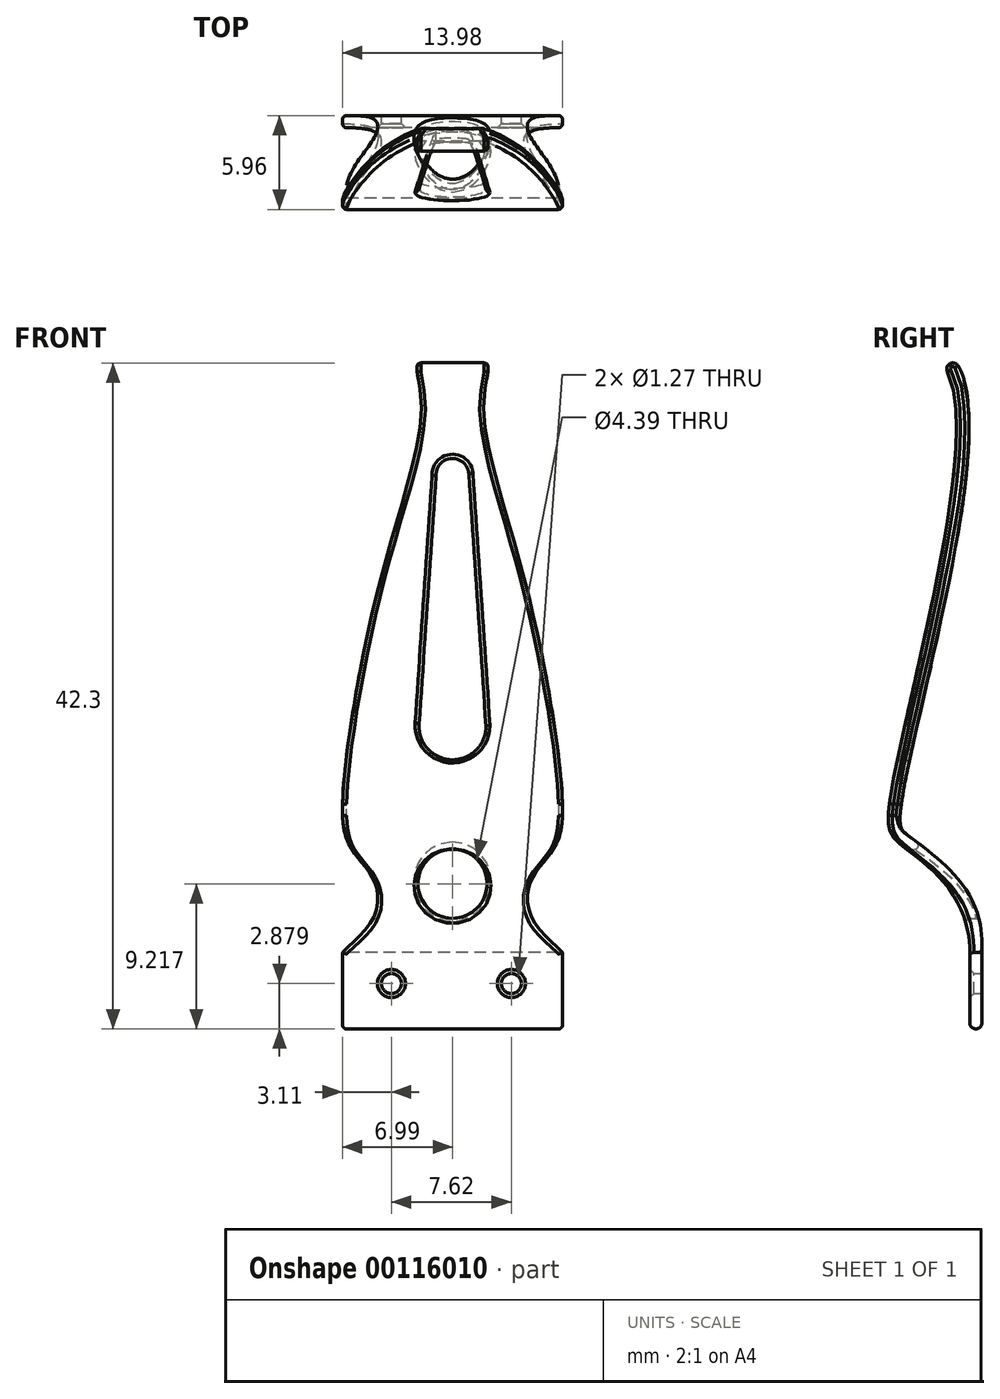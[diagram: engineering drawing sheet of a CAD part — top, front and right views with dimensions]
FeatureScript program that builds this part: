
annotation { "Feature Type Name" : "Feature", "Feature Type Description" : "" }
export const myFeature = defineFeature(function(context is Context, id is Id, definition is map)
    precondition{}
    {
        {
            var Q0;
            Q0=qCreatedBy(makeId("Right.planeOp"),FACE);
            var sketch = newSketch(context, id + "F0", { "sketchPlane" : qUnion([Q0])});
            skLineSegment(sketch, "E0", {"start": v(0, -14.27) * mm, "end": v(0, -9.42) * mm});
            skFitSpline(sketch, "E1", {"points": [v(0, -9.42) * mm, v(-4.26, -2.68) * mm, v(-5.11, 0) * mm, v(-1.6, 27.74) * mm], "startDerivative": vector(0, 39.78) * mm, "endDerivative": vector(-15.29, 20.66) * mm});
            skFitSpline(sketch, "E2.0", {"points": [v(0.76, -9.42) * mm, v(0.76, -8.5) * mm, v(0.46, -6.86) * mm, v(-0.6, -4.94) * mm, v(-1.72, -3.75) * mm, v(-2.6, -3) * mm, v(-3.2, -2.53) * mm, v(-3.72, -2.14) * mm, v(-4.1, -1.84) * mm, v(-4.25, -1.67) * mm, v(-4.32, -1.56) * mm, v(-4.36, -1.47) * mm, v(-4.4, -1.36) * mm, v(-4.43, -1.13) * mm, v(-4.43, -0.7) * mm, v(-4.34, 0.12) * mm, v(-4.08, 1.6) * mm, v(-3.57, 4.02) * mm, v(-2.75, 7.6) * mm, v(-1.87, 11.56) * mm, v(-1.04, 15.65) * mm, v(-0.39, 19.6) * mm, v(-0.1, 22.58) * mm, v(-0.07, 24.65) * mm, v(-0.18, 26.03) * mm, v(-0.45, 27.23) * mm, v(-0.78, 27.9) * mm, v(-1, 28.2) * mm]});
            skLineSegment(sketch, "E2.1", {"start": v(0.76, -14.27) * mm, "end": v(0.76, -9.42) * mm});
            skLineSegment(sketch, "E3", {"start": v(-1, 28.2) * mm, "end": v(-1.6, 27.74) * mm});
            skLineSegment(sketch, "E4", {"start": v(0.76, -14.27) * mm, "end": v(0, -14.27) * mm});
            skLineSegment(sketch, "E5", {"start": v(0, 1.37) * mm, "end": v(0, 29.32) * mm});
            skSolve(sketch);
        }
        {
            var Q0;
            Q0 = qSketchRegion(id + "F0", true);
            extrude(context, id + "F1", {"entities" : qUnion([Q0]), "endBound" : BoundingType.SYMMETRIC, "depth" : 13.97 * mm});
        }
        {
            var Q0;
            Q0=makeQuery(id+"F1.opExtrude","SWEPT_EDGE",EDGE,{"disambiguationData":[OSD([sQuery(id+"F0.wireOp",EDGE,"E1"),sQuery(id+"F0.wireOp",EDGE,"E3")])]});
            var Q1;
            Q1=makeQuery(id+"F1.opExtrude","SWEPT_EDGE",EDGE,{"disambiguationData":[OSD([sQuery(id+"F0.wireOp",EDGE,"E2.0"),sQuery(id+"F0.wireOp",EDGE,"E3")])]});
            var Q2;
            Q2=makeQuery(id+"F1.opExtrude","SWEPT_EDGE",EDGE,{"disambiguationData":[OSD([sQuery(id+"F0.wireOp",EDGE,"E0"),sQuery(id+"F0.wireOp",EDGE,"E4")])]});
            var Q3;
            Q3=makeQuery(id+"F1.opExtrude","SWEPT_EDGE",EDGE,{"disambiguationData":[OSD([sQuery(id+"F0.wireOp",EDGE,"E2.1"),sQuery(id+"F0.wireOp",EDGE,"E4")])]});
            fillet(context, id + "F2", {"entities" : qUnion([Q0, Q1, Q2, Q3]), "radius" : 0.38 * mm, "tangentPropagation" : true, "allowEdgeOverflow" : false});
        }
        {
            var Q0;
            Q0=makeQuery(id+"F1.opExtrude","SWEPT_FACE",FACE,{"disambiguationData":[OSD([sQuery(id+"F0.wireOp",EDGE,"E2.1")])]});
            var sketch = newSketch(context, id + "F3", { "sketchPlane" : qUnion([Q0])});
            skFitSpline(sketch, "E6", {"points": [v(-8.23, -11.23) * mm, v(-6.99, -9.42) * mm, v(-5.15, -7.43) * mm, v(-4.9, -5.05) * mm, v(-6.41, -2.84) * mm, v(-6.99, 0) * mm, v(-4.6, 14.19) * mm, v(-1.98, 25.5) * mm, v(-2.14, 28.2) * mm, v(0, 28.76) * mm], "startDerivative": vector(13.32, 22.9) * mm, "endDerivative": vector(34.07, 2.18) * mm});
            skFitSpline(sketch, "E7.MirrorCS", {"points": [v(8.23, -11.23) * mm, v(6.99, -9.42) * mm, v(5.15, -7.43) * mm, v(4.9, -5.05) * mm, v(6.41, -2.84) * mm, v(6.99, 0) * mm, v(4.6, 14.19) * mm, v(1.98, 25.5) * mm, v(2.14, 28.2) * mm, v(0, 28.76) * mm], "startDerivative": vector(-13.32, 22.9) * mm, "endDerivative": vector(-34.07, 2.18) * mm});
            skLineSegment(sketch, "E8", {"start": v(8.23, -11.23) * mm, "end": v(8.23, 29.3) * mm});
            skLineSegment(sketch, "E9", {"start": v(8.23, 29.3) * mm, "end": v(-8, 29.3) * mm});
            skLineSegment(sketch, "E10", {"start": v(-8, 29.3) * mm, "end": v(-8.23, -11.23) * mm});
            skCircle(sketch, "E11", {"center": v(0, 20.91) * mm, "radius": 1.05 * mm});
            skCircle(sketch, "E12", {"center": v(0, 4.94) * mm, "radius": 2.12 * mm});
            skLineSegment(sketch, "E13", {"start": v(-2.12, 4.94) * mm, "end": v(-1.05, 20.98) * mm});
            skLineSegment(sketch, "E14", {"start": v(1.05, 20.86) * mm, "end": v(2.12, 5.09) * mm});
            skCircle(sketch, "E15", {"center": v(0, -5.05) * mm, "radius": 2.2 * mm});
            skCircle(sketch, "E16", {"center": v(-3.74, -11.4) * mm, "radius": 0.64 * mm});
            skCircle(sketch, "E17", {"center": v(3.88, -11.4) * mm, "radius": 0.64 * mm});
            skLineSegment(sketch, "E18", {"start": v(-3.74, -11.4) * mm, "end": v(3.88, -11.4) * mm});
            skSolve(sketch);
        }
        {
            var Q0;
            {var subQ6=sQuery(id+"F3.wireOp",EDGE,"E8");Q0=makeQuery(id+"F3.imprint","IMPRINT",FACE,{"disambiguationData":[TD([[makeQuery(id+"F3.imprint","IMPRINT",EDGE,{"derivedFrom":subQ6}),1.0]])]});}
            var Q1;
            {var subQ0=sQuery(id+"F3.wireOp",EDGE,"E11");var subQ1=makeQuery(id+"F3.imprint","INTERSECT",VERTEX,{"derivedFrom":[subQ0,sQuery(id+"F3.wireOp",EDGE,"E13")]});Q1=makeQuery(id+"F3.imprint","IMPRINT",FACE,{"disambiguationData":[TD([[makeQuery(id+"F3.imprint","IMPRINT",EDGE,{"disambiguationData":[TD([[subQ1,-1.0]])],"derivedFrom":subQ0}),1.0]])]});}
            var Q2;
            {var subQ3=sQuery(id+"F3.wireOp",EDGE,"E14");Q2=makeQuery(id+"F3.imprint","IMPRINT",FACE,{"disambiguationData":[TD([[makeQuery(id+"F3.imprint","IMPRINT",EDGE,{"derivedFrom":subQ3}),-1.0]])]});}
            var Q3;
            {var subQ0=sQuery(id+"F3.wireOp",EDGE,"E12");var subQ1=makeQuery(id+"F3.imprint","INTERSECT",VERTEX,{"derivedFrom":[subQ0,sQuery(id+"F3.wireOp",EDGE,"E14")]});Q3=makeQuery(id+"F3.imprint","IMPRINT",FACE,{"disambiguationData":[TD([[makeQuery(id+"F3.imprint","IMPRINT",EDGE,{"disambiguationData":[TD([[subQ1,-1.0]])],"derivedFrom":subQ0}),1.0]])]});}
            var Q4;
            Q4=makeQuery(id+"F3.imprint","IMPRINT",FACE,{"disambiguationData":[TD([[makeQuery(id+"F3.imprint","IMPRINT",EDGE,{"derivedFrom":sQuery(id+"F3.wireOp",EDGE,"E15")}),1.0]])]});
            var Q5;
            Q5=makeQuery(id+"F3.imprint","IMPRINT",FACE,{"disambiguationData":[TD([[makeQuery(id+"F3.imprint","IMPRINT",EDGE,{"derivedFrom":sQuery(id+"F3.wireOp",EDGE,"E16")}),1.0]])]});
            var Q6;
            Q6=makeQuery(id+"F3.imprint","IMPRINT",FACE,{"disambiguationData":[TD([[makeQuery(id+"F3.imprint","IMPRINT",EDGE,{"derivedFrom":sQuery(id+"F3.wireOp",EDGE,"E17")}),1.0]])]});
            var Q7;
            Q7=sQuery(id+"F3.wireOp",EDGE,"E15");
            var Q8;
            Q8=sQuery(id+"F3.wireOp",EDGE,"E10");
            var Q9;
            Q9=sQuery(id+"F3.wireOp",EDGE,"E13");
            var Q10;
            Q10=sQuery(id+"F3.wireOp",EDGE,"E11");
            var Q11;
            Q11=sQuery(id+"F3.wireOp",EDGE,"E14");
            var Q12;
            Q12=sQuery(id+"F3.wireOp",EDGE,"E9");
            var Q13;
            Q13=sQuery(id+"F3.wireOp",EDGE,"E8");
            var Q14;
            Q14=sQuery(id+"F3.wireOp",EDGE,"E7.MirrorCS");
            var Q15;
            Q15=sQuery(id+"F3.wireOp",EDGE,"E6");
            var Q16;
            Q16=sQuery(id+"F3.wireOp",EDGE,"E12");
            extrude(context, id + "F4", {"entities" : qUnion([Q0, Q1, Q2, Q3, Q4, Q5, Q6]), "operationType" : NewBodyOperationType.REMOVE, "surfaceEntities" : qUnion([Q7, Q8, Q9, Q10, Q11, Q12, Q13, Q14, Q15, Q16]), "endBound" : BoundingType.SYMMETRIC, "oppositeDirection" : true, "depth" : 25.4 * mm});
        }
        {
            var Q0;
            Q0=makeQuery(id+"F4.boolean.opBoolean","INTERSECT",EDGE,{"disambiguationData":[OD(1.0)],"derivedFrom":[makeQuery(id+"F1.opExtrude","SWEPT_FACE",FACE,{"disambiguationData":[OSD([sQuery(id+"F0.wireOp",EDGE,"E1")])]}),makeQuery(id+"F4.opExtrude","SWEPT_FACE",FACE,{"disambiguationData":[OSD([sQuery(id+"F3.wireOp",EDGE,"E6")])]})]});
            var Q1;
            Q1=makeQuery(id+"F4.boolean.opBoolean","INTERSECT",EDGE,{"disambiguationData":[OD(1.0)],"derivedFrom":[makeQuery(id+"F1.opExtrude","SWEPT_FACE",FACE,{"disambiguationData":[OSD([sQuery(id+"F0.wireOp",EDGE,"E1")])]}),makeQuery(id+"F4.opExtrude","SWEPT_FACE",FACE,{"disambiguationData":[OSD([sQuery(id+"F3.wireOp",EDGE,"E7.MirrorCS")])]})]});
            var Q2;
            Q2=makeQuery(id+"F1.opExtrude","CAP_EDGE",EDGE,{"disambiguationData":[OSD([sQuery(id+"F0.wireOp",EDGE,"E1")])],"isStart":true});
            var Q3;
            Q3=makeQuery(id+"F4.boolean.opBoolean","INTERSECT",EDGE,{"disambiguationData":[OD(0.0)],"derivedFrom":[makeQuery(id+"F1.opExtrude","SWEPT_FACE",FACE,{"disambiguationData":[OSD([sQuery(id+"F0.wireOp",EDGE,"E1")])]}),makeQuery(id+"F4.opExtrude","SWEPT_FACE",FACE,{"disambiguationData":[OSD([sQuery(id+"F3.wireOp",EDGE,"E7.MirrorCS")])]})]});
            var Q4;
            Q4=makeQuery(id+"F1.opExtrude","CAP_EDGE",EDGE,{"disambiguationData":[OSD([sQuery(id+"F0.wireOp",EDGE,"E1")])],"isStart":false});
            var Q5;
            Q5=makeQuery(id+"F4.boolean.opBoolean","INTERSECT",EDGE,{"disambiguationData":[OD(0.0)],"derivedFrom":[makeQuery(id+"F1.opExtrude","SWEPT_FACE",FACE,{"disambiguationData":[OSD([sQuery(id+"F0.wireOp",EDGE,"E1")])]}),makeQuery(id+"F4.opExtrude","SWEPT_FACE",FACE,{"disambiguationData":[OSD([sQuery(id+"F3.wireOp",EDGE,"E6")])]})]});
            var Q6;
            Q6=makeQuery(id+"F1.opExtrude","CAP_EDGE",EDGE,{"disambiguationData":[OSD([sQuery(id+"F0.wireOp",EDGE,"E0")])],"isStart":false});
            var Q7;
            Q7=makeQuery(id+"F1.opExtrude","CAP_EDGE",EDGE,{"disambiguationData":[OSD([sQuery(id+"F0.wireOp",EDGE,"E0")])],"isStart":true});
            var Q8;
            Q8=makeQuery(id+"F4.boolean.opBoolean","INTERSECT",EDGE,{"derivedFrom":[makeQuery(id+"F1.opExtrude","SWEPT_FACE",FACE,{"disambiguationData":[OSD([sQuery(id+"F0.wireOp",EDGE,"E1")])]}),makeQuery(id+"F4.opExtrude","SWEPT_FACE",FACE,{"disambiguationData":[OSD([sQuery(id+"F3.wireOp",EDGE,"E15")])]})]});
            var Q9;
            Q9=makeQuery(id+"F4.boolean.opBoolean","INTERSECT",EDGE,{"derivedFrom":[makeQuery(id+"F1.opExtrude","SWEPT_FACE",FACE,{"disambiguationData":[OSD([sQuery(id+"F0.wireOp",EDGE,"E2.0")])]}),makeQuery(id+"F4.opExtrude","SWEPT_FACE",FACE,{"disambiguationData":[OSD([sQuery(id+"F3.wireOp",EDGE,"E15")])]})]});
            var Q10;
            Q10=makeQuery(id+"F4.boolean.opBoolean","INTERSECT",EDGE,{"derivedFrom":[makeQuery(id+"F1.opExtrude","SWEPT_FACE",FACE,{"disambiguationData":[OSD([sQuery(id+"F0.wireOp",EDGE,"E1")])]}),makeQuery(id+"F4.opExtrude","SWEPT_FACE",FACE,{"disambiguationData":[OSD([sQuery(id+"F3.wireOp",EDGE,"E12")])]})]});
            var Q11;
            Q11=makeQuery(id+"F4.boolean.opBoolean","INTERSECT",EDGE,{"derivedFrom":[makeQuery(id+"F1.opExtrude","SWEPT_FACE",FACE,{"disambiguationData":[OSD([sQuery(id+"F0.wireOp",EDGE,"E1")])]}),makeQuery(id+"F4.opExtrude","SWEPT_FACE",FACE,{"disambiguationData":[OSD([sQuery(id+"F3.wireOp",EDGE,"E13")])]})]});
            var Q12;
            Q12=makeQuery(id+"F4.boolean.opBoolean","INTERSECT",EDGE,{"derivedFrom":[makeQuery(id+"F1.opExtrude","SWEPT_FACE",FACE,{"disambiguationData":[OSD([sQuery(id+"F0.wireOp",EDGE,"E1")])]}),makeQuery(id+"F4.opExtrude","SWEPT_FACE",FACE,{"disambiguationData":[OSD([sQuery(id+"F3.wireOp",EDGE,"E14")])]})]});
            var Q13;
            Q13=makeQuery(id+"F4.boolean.opBoolean","INTERSECT",EDGE,{"derivedFrom":[makeQuery(id+"F1.opExtrude","SWEPT_FACE",FACE,{"disambiguationData":[OSD([sQuery(id+"F0.wireOp",EDGE,"E1")])]}),makeQuery(id+"F4.opExtrude","SWEPT_FACE",FACE,{"disambiguationData":[OSD([sQuery(id+"F3.wireOp",EDGE,"E11")])]})]});
            fillet(context, id + "F5", {"entities" : qUnion([Q0, Q1, Q2, Q3, Q4, Q5, Q6, Q7, Q8, Q9, Q10, Q11, Q12, Q13]), "radius" : 0.25 * mm, "tangentPropagation" : true, "allowEdgeOverflow" : false});
        }
        {
            var Q0;
            Q0=makeQuery(id+"F4.boolean.opBoolean","INTERSECT",EDGE,{"derivedFrom":[makeQuery(id+"F1.opExtrude","SWEPT_FACE",FACE,{"disambiguationData":[OSD([sQuery(id+"F0.wireOp",EDGE,"E0")])]}),makeQuery(id+"F4.opExtrude","SWEPT_FACE",FACE,{"disambiguationData":[OSD([sQuery(id+"F3.wireOp",EDGE,"E17")])]})]});
            var Q1;
            Q1=makeQuery(id+"F4.boolean.opBoolean","INTERSECT",EDGE,{"derivedFrom":[makeQuery(id+"F1.opExtrude","SWEPT_FACE",FACE,{"disambiguationData":[OSD([sQuery(id+"F0.wireOp",EDGE,"E0")])]}),makeQuery(id+"F4.opExtrude","SWEPT_FACE",FACE,{"disambiguationData":[OSD([sQuery(id+"F3.wireOp",EDGE,"E16")])]})]});
            chamfer(context, id + "F6", {"entities" : qUnion([Q0, Q1]), "width" : 0.25 * mm, "tangentPropagation" : true});
        }
    });
